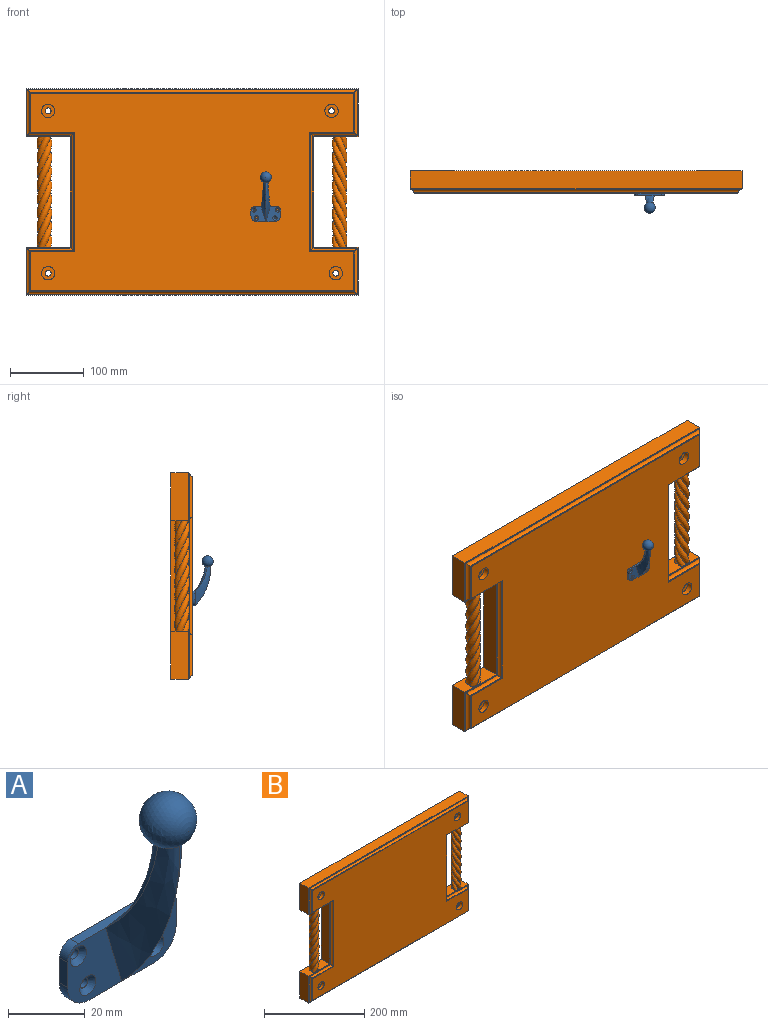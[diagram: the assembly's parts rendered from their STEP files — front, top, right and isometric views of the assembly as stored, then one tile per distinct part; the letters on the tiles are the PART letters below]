
ASSEMBLY  parts=2 mates=1
PART A: 23 faces, bbox 40x27.5x67.5 mm
  f0: plane 20x20mm, normal (0,-1,0), area 266.3mm2, adj f1,f3,f4,f8,f10,f16,f18,f19
  f1: plane 32x3mm, normal (0,0,1), area 96mm2, adj f0,f5,f6,f7,f8,f20
  f2: plane 8x3mm, normal (-1,0,0), area 24mm2, adj f5,f6,f7,f9
  f3: plane 24x3mm, normal (0,0,-1), area 72mm2, adj f0,f5,f6,f9,f10
  f4: plane 8x3mm, normal (1,0,0), area 24mm2, adj f0,f5,f8,f10
  f5: plane 40x20mm, normal (0,1,0), area 737.4mm2, adj f1,f2,f3,f4,f7,f8,f9,f10
  f6: plane 20x20mm, normal (0,-1,0), area 266.3mm2, adj f1,f2,f3,f7,f9,f12,f14,f21
  f7: cylinder r=4mm len=4mm, axis (0,1,0), area 18.8mm2, adj f1,f2,f5,f6
  f8: cylinder r=4mm len=4mm, axis (0,-1,0), area 18.8mm2, adj f0,f1,f4,f5
  f9: cylinder r=8mm len=8mm, axis (0,-1,0), area 37.7mm2, adj f2,f3,f5,f6
  f10: cylinder r=8mm len=8mm, axis (0,1,0), area 37.7mm2, adj f0,f3,f4,f5
  f11: cylinder r=1.5mm len=3mm, axis (0,-1,0), area 14.1mm2, adj f5,f12
  f12: cone r=1.5mm half-angle=45deg, axis (0,-1,0), area 30mm2, adj f6,f11
  f13: cylinder r=1.5mm len=3mm, axis (0,-1,0), area 14.1mm2, adj f5,f14
  f14: cone r=1.5mm half-angle=45deg, axis (0,-1,0), area 30mm2, adj f6,f13
  f15: cylinder r=1.5mm len=3mm, axis (0,-1,0), area 14.1mm2, adj f5,f16
  f16: cone r=1.5mm half-angle=45deg, axis (0,-1,0), area 30mm2, adj f0,f15
  f17: cylinder r=1.5mm len=3mm, axis (0,-1,0), area 14.1mm2, adj f5,f18
  f18: cone r=1.5mm half-angle=45deg, axis (0,-1,0), area 30mm2, adj f0,f17
  f19: bspline ~60x21.47mm, area 493.5mm2, adj f0,f20,f21,f22
  f20: bspline ~33.69x16.57mm, area 393.8mm2, adj f1,f19,f21,f22
  f21: bspline ~60x21.47mm, area 493.5mm2, adj f6,f19,f20,f22
  f22: sphere r=7.5mm, area 663mm2, adj f19,f20,f21
PART B: 72 faces, bbox 450x32.4x280 mm
  f0: plane 450x24.1mm, normal (0,0,1), area 10845.5mm2, adj f2,f3,f12,f48
  f1: plane 65x24.1mm, normal (1,0,0), area 1566.6mm2, adj f8,f9,f12,f48
  f2: plane 65x24.1mm, normal (1,0,0), area 1566.6mm2, adj f0,f11,f12,f48
  f3: plane 65x24.1mm, normal (-1,0,0), area 1566.6mm2, adj f0,f4,f12,f48
  f4: plane 60x24.1mm, normal (0,0,-1), area 1189mm2, adj f3,f5,f12,f48,f64,f65,f66,f67
  f5: plane 150x24.1mm, normal (-1,0,0), area 3615.2mm2, adj f4,f6,f12,f48
  f6: plane 60x24.1mm, normal (0,0,1), area 1189mm2, adj f5,f7,f12,f48,f64,f65,f66,f67
  f7: plane 65x24.1mm, normal (-1,0,0), area 1566.6mm2, adj f6,f8,f12,f48
  f8: plane 450x24.1mm, normal (0,0,-1), area 10845.5mm2, adj f1,f7,f12,f48
  f9: plane 60x24.1mm, normal (0,0,1), area 1189mm2, adj f1,f10,f12,f48,f68,f69,f70,f71
  f10: plane 150x24.1mm, normal (1,0,0), area 3615.2mm2, adj f9,f11,f12,f48
  f11: plane 60x24.1mm, normal (0,0,-1), area 1189mm2, adj f2,f10,f12,f48,f68,f69,f70,f71
  f12: plane 450x280mm, normal (0,1,0), area 107798.9mm2, adj f0,f1,f2,f3,f4,f5,f6,f7
  f13: cylinder r=5mm len=448mm, axis (-1,0,0), area 2589.2mm2, adj f14,f16,f19,f50
  f14: plane 448x1mm, normal (0,0,-1), area 448mm2, adj f13,f17,f20,f48
  f15: plane 438.2x1mm, normal (0,0,-1), area 438.2mm2, adj f18,f21,f50,f51
  f16: cylinder r=5mm len=63mm, axis (0,0,1), area 340.6mm2, adj f13,f17,f24,f50
  f17: plane 63x1mm, normal (-1,0,0), area 63mm2, adj f14,f16,f23,f48
  f18: plane 53.2x1mm, normal (-1,0,0), area 53.2mm2, adj f15,f22,f50,f51
  f19: cylinder r=5mm len=63mm, axis (0,0,-1), area 340.6mm2, adj f13,f20,f25,f50
  f20: plane 63x1mm, normal (1,0,0), area 63mm2, adj f14,f19,f26,f48
  f21: plane 53.2x1mm, normal (1,0,0), area 53.2mm2, adj f15,f27,f50,f51
  f22: plane 60x1mm, normal (0,0,1), area 60mm2, adj f18,f28,f50,f51
  f23: plane 60x1mm, normal (0,0,1), area 60mm2, adj f17,f24,f29,f48
  f24: cylinder r=5mm len=63.9mm, axis (1,0,0), area 350.4mm2, adj f16,f23,f30,f50
  f25: cylinder r=5mm len=63.9mm, axis (1,0,0), area 350.4mm2, adj f19,f26,f33,f50
  f26: plane 60x1mm, normal (0,0,1), area 60mm2, adj f20,f25,f32,f48
  f27: plane 60x1mm, normal (0,0,1), area 60mm2, adj f21,f31,f50,f51
  f28: plane 161.8x1mm, normal (-1,0,0), area 161.8mm2, adj f22,f36,f50,f51
  f29: plane 152x1mm, normal (-1,0,0), area 152mm2, adj f23,f30,f35,f48
  f30: cylinder r=5mm len=159.8mm, axis (0,0,1), area 915.1mm2, adj f24,f29,f34,f50
  f31: plane 161.8x1mm, normal (1,0,0), area 161.8mm2, adj f27,f37,f50,f51
  f32: plane 152x1mm, normal (1,0,0), area 152mm2, adj f26,f33,f38,f48
  f33: cylinder r=5mm len=159.8mm, axis (0,0,-1), area 915.1mm2, adj f25,f32,f39,f50
  f34: cylinder r=5mm len=63.9mm, axis (-1,0,0), area 350.4mm2, adj f30,f35,f40,f50
  f35: plane 60x1mm, normal (0,0,-1), area 60mm2, adj f29,f34,f41,f48
  f36: plane 60x1mm, normal (0,0,-1), area 60mm2, adj f28,f42,f50,f51
  f37: plane 60x1mm, normal (0,0,-1), area 60mm2, adj f31,f45,f50,f51
  f38: plane 60x1mm, normal (0,0,-1), area 60mm2, adj f32,f39,f44,f48
  f39: cylinder r=5mm len=63.9mm, axis (-1,0,0), area 350.4mm2, adj f33,f38,f43,f50
  f40: cylinder r=5mm len=63mm, axis (0,0,1), area 340.6mm2, adj f34,f41,f46,f50
  f41: plane 63x1mm, normal (-1,0,0), area 63mm2, adj f35,f40,f47,f48
  f42: plane 53.2x1mm, normal (-1,0,0), area 53.2mm2, adj f36,f49,f50,f51
  f43: cylinder r=5mm len=63mm, axis (0,0,-1), area 340.6mm2, adj f39,f44,f46,f50
  f44: plane 63x1mm, normal (1,0,0), area 63mm2, adj f38,f43,f47,f48
  f45: plane 53.2x1mm, normal (1,0,0), area 53.2mm2, adj f37,f49,f50,f51
  f46: cylinder r=5mm len=448mm, axis (1,0,0), area 2589.2mm2, adj f40,f43,f47,f50
  f47: plane 448x1mm, normal (0,0,1), area 448mm2, adj f41,f44,f46,f48
  f48: plane 450x280mm, normal (0,-1,0), area 1696mm2, adj f0,f1,f2,f3,f4,f5,f6,f7
  f49: plane 438.2x1mm, normal (0,0,1), area 438.2mm2, adj f42,f45,f50,f51
  f50: plane 440.2x270.2mm, normal (0,-1,0), area 1656.8mm2, adj f13,f15,f16,f18,f19,f21,f22,f24
  f51: plane 438.2x268.2mm, normal (0,-1,0), area 97093.1mm2, adj f15,f18,f21,f22,f27,f28,f31,f36
  f52: cylinder r=4mm len=22mm, axis (0,-1,0), area 552.9mm2, adj f12,f53
  f53: plane 18x18mm, normal (0,-1,0), area 204.2mm2, adj f52,f54
  f54: cylinder r=9mm len=18mm, axis (0,-1,0), area 452.4mm2, adj f51,f53
  f55: cylinder r=4mm len=22mm, axis (0,-1,0), area 552.9mm2, adj f12,f56
  f56: plane 18x18mm, normal (0,-1,0), area 204.2mm2, adj f55,f57
  f57: cylinder r=9mm len=18mm, axis (0,-1,0), area 452.4mm2, adj f51,f56
  f58: cylinder r=4mm len=22mm, axis (0,-1,0), area 552.9mm2, adj f12,f59
  f59: plane 18x18mm, normal (0,-1,0), area 204.2mm2, adj f58,f60
  f60: cylinder r=9mm len=18mm, axis (0,-1,0), area 452.4mm2, adj f51,f59
  f61: cylinder r=4mm len=22mm, axis (0,-1,0), area 552.9mm2, adj f12,f62
  f62: plane 18x18mm, normal (0,-1,0), area 204.2mm2, adj f61,f63
  f63: cylinder r=9mm len=18mm, axis (0,-1,0), area 452.4mm2, adj f51,f62
  f64: bspline ~150x32.43mm, area 2457.6mm2, adj f4,f6,f65,f67
  f65: bspline ~150x32.43mm, area 2457.6mm2, adj f4,f6,f64,f66
  f66: bspline ~150x32.43mm, area 2457.6mm2, adj f4,f6,f65,f67
  f67: bspline ~150x32.43mm, area 2457.6mm2, adj f4,f6,f64,f66
  f68: bspline ~150x32.43mm, area 2457.6mm2, adj f9,f11,f69,f71
  f69: bspline ~150x32.43mm, area 2457.6mm2, adj f9,f11,f68,f70
  f70: bspline ~150x32.43mm, area 2457.6mm2, adj f9,f11,f69,f71
  f71: bspline ~150x32.43mm, area 2457.6mm2, adj f9,f11,f68,f70
PLACE A t=(58.15,36.07,-15.55)mm
PLACE B t=(-41.82,69.07,14.66)mm
MATE planar A.f5 <-> B.f51  axis (0,1,0) through (58.15,39.07,-15.35)mm
